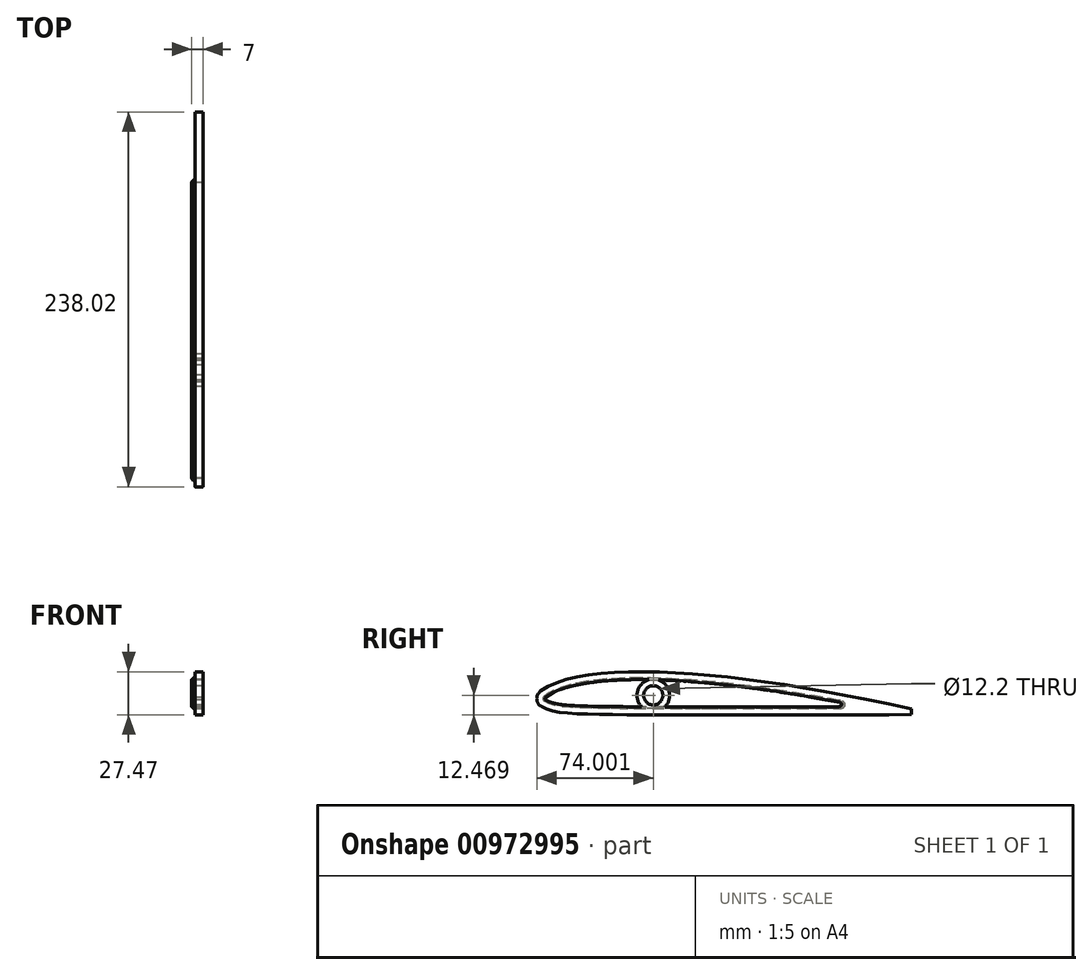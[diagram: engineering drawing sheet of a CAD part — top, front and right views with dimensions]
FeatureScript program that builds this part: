
annotation { "Feature Type Name" : "Feature", "Feature Type Description" : "" }
export const myFeature = defineFeature(function(context is Context, id is Id, definition is map)
    precondition{}
    {
        {
            var Q0;
            Q0=qCreatedBy(makeId("Right.planeOp"),FACE);
            var sketch = newSketch(context, id + "F0", { "sketchPlane" : qUnion([Q0])});
            skLineSegment(sketch, "E0", {"start": v(0, 0) * mm, "end": v(238.13, 0) * mm, "construction": true});
            skLineSegment(sketch, "E1", {"start": v(0, 0) * mm, "end": v(0, 0) * mm, "construction": true});
            skLineSegment(sketch, "E2", {"start": v(238, 3.78) * mm, "end": v(238, 0) * mm});
            skArc(sketch, "E3", {"start": v(2.42, 14.91) * mm, "mid": v(0, 9.87) * mm, "end": v(2.87, 5.07) * mm});
            skFitSpline(sketch, "E4", {"points": [v(238, 3.78) * mm, v(106.78, 25.25) * mm, v(33.8, 25.33) * mm, v(2.42, 14.91) * mm], "startDerivative": vector(-337.3, 72.63) * mm, "endDerivative": vector(-98.74, -71.57) * mm});
            skFitSpline(sketch, "E5", {"points": [v(238, 0) * mm, v(38.76, 0.2) * mm, v(2.87, 5.07) * mm], "startDerivative": vector(-331.95, -0.25) * mm, "endDerivative": vector(-67.54, 40.03) * mm});
            skSolve(sketch);
        }
        {
            var Q0;
            Q0=makeQuery(id+"F0.imprint","IMPRINT",FACE,{"disambiguationData":[TD([[makeQuery(id+"F0.imprint","IMPRINT",EDGE,{"derivedFrom":sQuery(id+"F0.wireOp",EDGE,"E2")}),-1.0]])]});
            extrude(context, id + "F1", {"entities" : qUnion([Q0]), "depth" : 5 * mm, "offsetDistance" : 25 * mm});
        }
        {
            var Q0;
            Q0=qCreatedBy(makeId("Right.planeOp"),FACE);
            var sketch = newSketch(context, id + "F2", { "sketchPlane" : qUnion([Q0])});
            skCircle(sketch, "E6", {"center": v(74, 12.26) * mm, "radius": 7.55 * mm});
            skLineSegment(sketch, "E7", {"start": v(27.72, 27.26) * mm, "end": v(191.9, 27.26) * mm, "construction": true});
            skLineSegment(sketch, "E8", {"start": v(56.37, 12.26) * mm, "end": v(199.63, 12.26) * mm, "construction": true});
            skLineSegment(sketch, "E9", {"start": v(54.7, 18.66) * mm, "end": v(212.58, 18.66) * mm, "construction": true});
            skSolve(sketch);
        }
        {
            var Q0;
            Q0=qSketchRegion(id+"F2",true);
            extrude(context, id + "F3", {"entities" : qUnion([Q0]), "operationType" : NewBodyOperationType.REMOVE, "endBound" : BoundingType.THROUGH_ALL, "depth" : 25 * mm, "offsetDistance" : 25 * mm, "hasSecondDirection" : true, "secondDirectionBound" : BoundingType.THROUGH_ALL, "secondDirectionOppositeDirection" : true, "secondDirectionDepth" : 25 * mm});
        }
        {
            var Q0;
            Q0=qCreatedBy(makeId("Right.planeOp"),FACE);
            var sketch = newSketch(context, id + "F4", { "sketchPlane" : qUnion([Q0])});
            skFitSpline(sketch, "E10.0", {"points": [v(237.16, -0.13) * mm, v(223.14, 2.89) * mm, v(202.94, 7) * mm, v(177.56, 11.64) * mm, v(159.27, 14.68) * mm, v(141.7, 17.28) * mm, v(124.83, 19.43) * mm, v(108.61, 21.13) * mm, v(93.02, 22.37) * mm, v(78.16, 23.13) * mm, v(64.12, 23.35) * mm, v(51.04, 23.01) * mm, v(39.03, 22.08) * mm, v(28.2, 20.52) * mm, v(18.73, 18.3) * mm, v(10.77, 15.4) * mm, v(6.58, 12.99) * mm, v(4.77, 11.67) * mm]});
            skFitSpline(sketch, "E10.1", {"points": [v(238, 4) * mm, v(224.17, 3.99) * mm, v(196.38, 3.94) * mm, v(155.67, 3.84) * mm, v(123.67, 3.79) * mm, v(99.89, 3.79) * mm, v(83.13, 3.82) * mm, v(67.63, 3.88) * mm, v(55.88, 3.98) * mm, v(47.28, 4.07) * mm, v(41.25, 4.16) * mm, v(35.66, 4.26) * mm, v(30.52, 4.39) * mm, v(25.84, 4.56) * mm, v(20.17, 4.88) * mm, v(14.16, 5.5) * mm, v(9.54, 6.52) * mm, v(6.65, 7.58) * mm, v(5.46, 8.19) * mm, v(4.91, 8.5) * mm]});
            skArc(sketch, "E10.2", {"start": v(4.77, 11.67) * mm, "mid": v(3.99, 10.05) * mm, "end": v(4.91, 8.5) * mm});
            skArc(sketch, "E11.0", {"start": v(83.28, 3.82) * mm, "mid": v(86.52, 11.46) * mm, "end": v(84.28, 19.45) * mm});
            skLineSegment(sketch, "E12.0", {"start": v(59.94, 23.2) * mm, "end": v(10.02, 6.48) * mm});
            skLineSegment(sketch, "E13.0", {"start": v(63.49, 19.12) * mm, "end": v(20.94, 4.87) * mm});
            skLineSegment(sketch, "E14.0", {"start": v(84.28, 19.45) * mm, "end": v(146.9, 3.83) * mm});
            skLineSegment(sketch, "E15.0", {"start": v(93.69, 22.26) * mm, "end": v(167.39, 3.87) * mm});
            skFitSpline(sketch, "E16.trimOffspring", {"points": [v(238, 4) * mm, v(224.17, 3.99) * mm, v(196.38, 3.94) * mm, v(155.67, 3.84) * mm, v(123.67, 3.79) * mm, v(99.89, 3.79) * mm, v(83.13, 3.82) * mm, v(67.63, 3.88) * mm, v(55.88, 3.98) * mm, v(47.28, 4.07) * mm, v(41.25, 4.16) * mm, v(35.66, 4.26) * mm, v(30.52, 4.39) * mm, v(25.84, 4.56) * mm, v(20.17, 4.88) * mm, v(14.16, 5.5) * mm, v(9.54, 6.52) * mm, v(6.65, 7.58) * mm, v(5.46, 8.19) * mm, v(4.91, 8.5) * mm]});
            skFitSpline(sketch, "E17.trimOffspring", {"points": [v(237.16, -0.13) * mm, v(223.14, 2.89) * mm, v(202.94, 7) * mm, v(177.56, 11.64) * mm, v(159.27, 14.68) * mm, v(141.7, 17.28) * mm, v(124.83, 19.43) * mm, v(108.61, 21.13) * mm, v(93.02, 22.37) * mm, v(78.16, 23.13) * mm, v(64.12, 23.35) * mm, v(51.04, 23.01) * mm, v(39.03, 22.08) * mm, v(28.2, 20.52) * mm, v(18.73, 18.3) * mm, v(10.77, 15.4) * mm, v(6.58, 12.99) * mm, v(4.77, 11.67) * mm]});
            skFitSpline(sketch, "E18.trimOffspring", {"points": [v(238, 4) * mm, v(224.17, 3.99) * mm, v(196.38, 3.94) * mm, v(155.67, 3.84) * mm, v(123.67, 3.79) * mm, v(99.89, 3.79) * mm, v(83.13, 3.82) * mm, v(67.63, 3.88) * mm, v(55.88, 3.98) * mm, v(47.28, 4.07) * mm, v(41.25, 4.16) * mm, v(35.66, 4.26) * mm, v(30.52, 4.39) * mm, v(25.84, 4.56) * mm, v(20.17, 4.88) * mm, v(14.16, 5.5) * mm, v(9.54, 6.52) * mm, v(6.65, 7.58) * mm, v(5.46, 8.19) * mm, v(4.91, 8.5) * mm]});
            skArc(sketch, "E19.trimOffspring", {"start": v(63.49, 19.12) * mm, "mid": v(61.48, 11.33) * mm, "end": v(64.62, 3.91) * mm});
            skFitSpline(sketch, "E20.trimOffspring", {"points": [v(238, 4) * mm, v(224.17, 3.99) * mm, v(196.38, 3.94) * mm, v(155.67, 3.84) * mm, v(123.67, 3.79) * mm, v(99.89, 3.79) * mm, v(83.13, 3.82) * mm, v(67.63, 3.88) * mm, v(55.88, 3.98) * mm, v(47.28, 4.07) * mm, v(41.25, 4.16) * mm, v(35.66, 4.26) * mm, v(30.52, 4.39) * mm, v(25.84, 4.56) * mm, v(20.17, 4.88) * mm, v(14.16, 5.5) * mm, v(9.54, 6.52) * mm, v(6.65, 7.58) * mm, v(5.46, 8.19) * mm, v(4.91, 8.5) * mm]});
            skSolve(sketch);
        }
        {
            var Q0;
            Q0=qSketchRegion(id+"F4",true);
            extrude(context, id + "F5", {"entities" : qUnion([Q0]), "operationType" : NewBodyOperationType.ADD, "oppositeDirection" : true, "depth" : 2 * mm, "offsetDistance" : 25 * mm, "hasDraft" : true, "draftAngle" : 5 * degree, "draftPullDirection" : true});
        }
        {
            var Q0;
            Q0=makeQuery(id+"F5.opExtrude","SWEPT_EDGE",EDGE,{"disambiguationData":[OSD([sQuery(id+"F4.wireOp",EDGE,"E10.0"),sQuery(id+"F4.wireOp",EDGE,"E15.0")])]});
            var Q1;
            Q1=makeQuery(id+"F5.opExtrude","SWEPT_EDGE",EDGE,{"disambiguationData":[OSD([sQuery(id+"F4.wireOp",EDGE,"E11.0"),sQuery(id+"F4.wireOp",EDGE,"E14.0")])]});
            var Q2;
            Q2=makeQuery(id+"F5.opExtrude","SWEPT_EDGE",EDGE,{"disambiguationData":[OSD([sQuery(id+"F4.wireOp",EDGE,"E11.0"),sQuery(id+"F4.wireOp",EDGE,"E18.trimOffspring")])]});
            var Q3;
            Q3=makeQuery(id+"F5.opExtrude","SWEPT_EDGE",EDGE,{"disambiguationData":[OSD([sQuery(id+"F4.wireOp",EDGE,"E12.0"),sQuery(id+"F4.wireOp",EDGE,"E17.trimOffspring")])]});
            var Q4;
            Q4=makeQuery(id+"F5.opExtrude","SWEPT_EDGE",EDGE,{"disambiguationData":[OSD([sQuery(id+"F4.wireOp",EDGE,"E13.0"),sQuery(id+"F4.wireOp",EDGE,"E19.trimOffspring")])]});
            var Q5;
            Q5=makeQuery(id+"F5.opExtrude","SWEPT_EDGE",EDGE,{"disambiguationData":[OSD([sQuery(id+"F4.wireOp",EDGE,"E13.0"),sQuery(id+"F4.wireOp",EDGE,"E16.trimOffspring")])]});
            var Q6;
            Q6=makeQuery(id+"F5.opExtrude","SWEPT_EDGE",EDGE,{"disambiguationData":[OSD([sQuery(id+"F4.wireOp",EDGE,"E12.0"),sQuery(id+"F4.wireOp",EDGE,"E20.trimOffspring")])]});
            var Q7;
            Q7=makeQuery(id+"F5.opExtrude","SWEPT_EDGE",EDGE,{"disambiguationData":[OSD([sQuery(id+"F4.wireOp",EDGE,"E16.trimOffspring"),sQuery(id+"F4.wireOp",EDGE,"E19.trimOffspring")])]});
            var Q8;
            Q8=makeQuery(id+"F5.opExtrude","SWEPT_EDGE",EDGE,{"disambiguationData":[OSD([sQuery(id+"F4.wireOp",EDGE,"E14.0"),sQuery(id+"F4.wireOp",EDGE,"E18.trimOffspring")])]});
            var Q9;
            Q9=makeQuery(id+"F5.opExtrude","SWEPT_EDGE",EDGE,{"disambiguationData":[OSD([sQuery(id+"F4.wireOp",EDGE,"E10.1"),sQuery(id+"F4.wireOp",EDGE,"E15.0")])]});
            var Q10;
            Q10=makeQuery(id+"F5.opExtrude","SWEPT_EDGE",EDGE,{"disambiguationData":[OSD([sQuery(id+"F4.wireOp",EDGE,"E10.0"),sQuery(id+"F4.wireOp",EDGE,"E10.1")])]});
            fillet(context, id + "F6", {"entities" : qUnion([Q0, Q1, Q2, Q3, Q4, Q5, Q6, Q7, Q8, Q9, Q10]), "radius" : 2.5 * mm, "tangentPropagation" : true, "allowEdgeOverflow" : false});
        }
        {
            var Q0;
            Q0=makeQuery(id+"F5.opExtrude","CAP_FACE",FACE,{"disambiguationData":[OSD([sQuery(id+"F4.wireOp",EDGE,"E10.0"),sQuery(id+"F4.wireOp",EDGE,"E10.1"),sQuery(id+"F4.wireOp",EDGE,"E15.0")])],"isStart":false});
            var Q1;
            Q1=makeQuery(id+"F5.opExtrude","CAP_FACE",FACE,{"disambiguationData":[OSD([sQuery(id+"F4.wireOp",EDGE,"E11.0"),sQuery(id+"F4.wireOp",EDGE,"E14.0"),sQuery(id+"F4.wireOp",EDGE,"E18.trimOffspring")])],"isStart":false});
            var Q2;
            Q2=makeQuery(id+"F5.opExtrude","CAP_FACE",FACE,{"disambiguationData":[OSD([sQuery(id+"F4.wireOp",EDGE,"E13.0"),sQuery(id+"F4.wireOp",EDGE,"E16.trimOffspring"),sQuery(id+"F4.wireOp",EDGE,"E19.trimOffspring")])],"isStart":false});
            var Q3;
            Q3=makeQuery(id+"F5.opExtrude","CAP_FACE",FACE,{"disambiguationData":[OSD([sQuery(id+"F4.wireOp",EDGE,"E10.2"),sQuery(id+"F4.wireOp",EDGE,"E12.0"),sQuery(id+"F4.wireOp",EDGE,"E17.trimOffspring"),sQuery(id+"F4.wireOp",EDGE,"E20.trimOffspring")])],"isStart":false});
            chamfer(context, id + "F7", {"entities" : qUnion([Q0, Q1, Q2, Q3]), "width" : 1 * mm, "tangentPropagation" : true});
        }
        {
            var Q0;
            Q0=makeQuery(id+"F5.opExtrude","CAP_FACE",FACE,{"disambiguationData":[OSD([sQuery(id+"F4.wireOp",EDGE,"E10.0"),sQuery(id+"F4.wireOp",EDGE,"E10.1"),sQuery(id+"F4.wireOp",EDGE,"E15.0")])],"isStart":false});
            var Q1;
            Q1=makeQuery(id+"F5.opExtrude","CAP_FACE",FACE,{"disambiguationData":[OSD([sQuery(id+"F4.wireOp",EDGE,"E11.0"),sQuery(id+"F4.wireOp",EDGE,"E14.0"),sQuery(id+"F4.wireOp",EDGE,"E18.trimOffspring")])],"isStart":false});
            var Q2;
            Q2=makeQuery(id+"F5.opExtrude","CAP_FACE",FACE,{"disambiguationData":[OSD([sQuery(id+"F4.wireOp",EDGE,"E13.0"),sQuery(id+"F4.wireOp",EDGE,"E16.trimOffspring"),sQuery(id+"F4.wireOp",EDGE,"E19.trimOffspring")])],"isStart":false});
            var Q3;
            Q3=makeQuery(id+"F5.opExtrude","CAP_FACE",FACE,{"disambiguationData":[OSD([sQuery(id+"F4.wireOp",EDGE,"E10.2"),sQuery(id+"F4.wireOp",EDGE,"E12.0"),sQuery(id+"F4.wireOp",EDGE,"E17.trimOffspring"),sQuery(id+"F4.wireOp",EDGE,"E20.trimOffspring")])],"isStart":false});
            extrude(context, id + "F8", {"entities" : qUnion([Q0, Q1, Q2, Q3]), "operationType" : NewBodyOperationType.REMOVE, "endBound" : BoundingType.THROUGH_ALL, "oppositeDirection" : true, "depth" : 25 * mm, "offsetDistance" : 25 * mm});
        }
        {
            var Q0;
            Q0=makeQuery(id+"F1.opExtrude","CAP_FACE",FACE,{"disambiguationData":[OSD([sQuery(id+"F0.wireOp",EDGE,"E2"),sQuery(id+"F0.wireOp",EDGE,"E3"),sQuery(id+"F0.wireOp",EDGE,"E4"),sQuery(id+"F0.wireOp",EDGE,"E5")])],"isStart":true});
            var sketch = newSketch(context, id + "F9", { "sketchPlane" : qUnion([Q0])});
            skCircle(sketch, "E21", {"center": v(-74, 12.26) * mm, "radius": 6.1 * mm});
            skCircle(sketch, "E22", {"center": v(-74, 12.26) * mm, "radius": 10.36 * mm});
            skSolve(sketch);
        }
        {
            var Q0;
            Q0 = qSketchRegion(id + "F9", true);
            var Q1;
            Q1=makeQuery(id+"F1.opExtrude","CAP_FACE",FACE,{"disambiguationData":[OSD([sQuery(id+"F0.wireOp",EDGE,"E2"),sQuery(id+"F0.wireOp",EDGE,"E3"),sQuery(id+"F0.wireOp",EDGE,"E4"),sQuery(id+"F0.wireOp",EDGE,"E5")])],"isStart":false});
            extrude(context, id + "F10", {"entities" : qUnion([Q0]), "operationType" : NewBodyOperationType.ADD, "endBound" : BoundingType.UP_TO_SURFACE, "oppositeDirection" : true, "depth" : 25 * mm, "endBoundEntityFace" : qUnion([Q1]), "offsetDistance" : 25 * mm});
        }
    });
